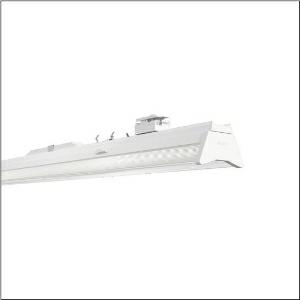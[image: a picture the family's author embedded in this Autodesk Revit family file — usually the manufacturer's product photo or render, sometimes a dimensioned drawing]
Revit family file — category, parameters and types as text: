
# Revit family: licross_r__21_performance_ho_52tm16dn4e5m_a06b
name_source: partatom
category: Lighting Fixtures
units: mm (PartAtom-declared; Revit-internal decimal feet)

## family parameters
Cut with Voids When Loaded = No
Host = Face
Light Source = No
Part Type = Normal
Room Calculation Point = No
Round Connector Dimension = Use Diameter
Shared = No

## types (1)
- --- (1 x LED, 14870 lm, 84.9 W, 4000K)
    Apparent Load = 85 VA
    CIE Flux Codes = 63 87 95 78 100
    Color Rendering = 80
    Color Temperature = 4000K
    Default Elevation = 1800 mm
    Description = Licross® 21 Performance HO, luminaire insert, of sheet steel, galvanised, coil coated, white, length: 1.500mm, width: 120mm, height: 123mm, LED rated luminous flux: 14.870lm, light colour: 840, control gear: DALI 2, control gear: ECG DALI, with plug, 5-pole, with phase selection, mains connection: 220..240V, AC, 50/60Hz, halogen-free wiring, primary light control with lens, of plastic, primary optical cover: cover, of PMMA, light emission: direct/indirect distribution, primary light characteristic: symmetric, protection rating (complete): IP40, insulation class (complete): insulation class I (protective earthing), certification: CE, ENEC, UKCA, protection symbol: D if used in an environment without relevant dust loads with corresponding accessories, impact resistance: IK06, permissible ambient temperature for indoor applications: -25..+35°C, corresponds to IFS (International Featured Standards) requirements for safety and quality in the food industry, reducing of maximum allowable ambient temperature of 5°C with ceiling mounting, LABS conformity tested according to VDMA 24364:2018-05, packaging unit: 1 piece
    Height = 114 mm
    Lamp = 1 x LED
    Lamp Light Flux = 14870 lm
    Lamp Power = 84.9 W
    Lamp count = 1
    Length = 1500 mm
    Luminous efficacy = 175 lm/W
    Manufacturer = Siteco
    ModVariant = No
    Model = 52TM16DN4E5M
    Mounting Place = Ceiling
    Mounting Type = Pendant
    Number of Poles = 1
    OnlyDefault = Yes
    Power Factor = 1
    Product Name = Licross® 21 Performance HO
    Product group = luminaire insert
    ProductGroupID = 902
    Protection Class = Protection class I
    Protection Degree = IP 40
    RLX_Detail_Level = 1
    RlxData = <blob elided: 34113 chars, md5=32a3b933>
    Socket = socket
    Standby Power = 0 W
    System Light Flux = 14870 lm
    System Power = 85 W
    Type Comments = factory setting: luminous flux: 100 % | dim-lin: 254 | 484 mA
    Type Image = l_1256138.jpg
    URL = http://relux.com
    VarID = @adj_039669
    Voltage = 0 V
    Weight = 0.00 kg
    Width = 120 mm

## geometry (parser evidence)
native form markers: Blend x4, Sweep x13
no freeform markers — native parametric forms only
